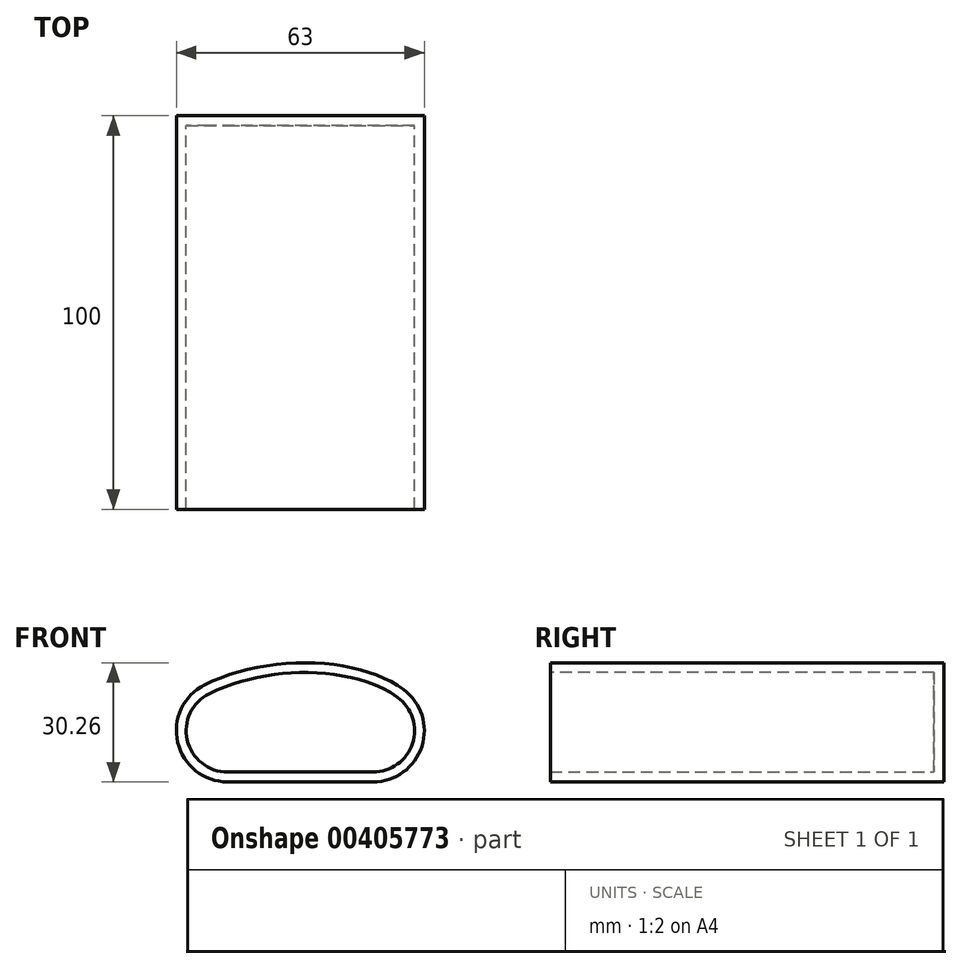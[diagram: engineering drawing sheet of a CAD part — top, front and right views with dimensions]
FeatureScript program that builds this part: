
annotation { "Feature Type Name" : "Feature", "Feature Type Description" : "" }
export const myFeature = defineFeature(function(context is Context, id is Id, definition is map)
    precondition{}
    {
        {
            var Q0;
            Q0=qCreatedBy(makeId("Front.planeOp"),FACE);
            var sketch = newSketch(context, id + "F0", { "sketchPlane" : qUnion([Q0])});
            skLineSegment(sketch, "E0", {"start": v(-15.79, 0) * mm, "end": v(21.21, 0) * mm});
            skCircle(sketch, "E1", {"center": v(-15.79, 0) * mm, "radius": 13 * mm});
            skCircle(sketch, "E2", {"center": v(21.21, 0) * mm, "radius": 13 * mm});
            skLineSegment(sketch, "E3", {"start": v(-15.79, 13) * mm, "end": v(21.21, 13) * mm});
            skLineSegment(sketch, "E4", {"start": v(2.71, 13) * mm, "end": v(2.71, -19) * mm});
            skPoint(sketch, "E4.endSnap0", {"position": v(2.71, 0) * mm});
            skEllipticalArc(sketch, "E5", {});
            skEllipse(sketch, "E6", {"center": v(2.71, -3) * mm, "majorRadius": 38.06 * mm, "minorRadius": 19.07 * mm, "majorAxis": v(-1, 0)});
            skLineSegment(sketch, "E7", {"start": v(-15.79, -13) * mm, "end": v(21.21, -13) * mm});
            const initialGuessF0  = {"E5": [0, -0.0030846775043755774, -0.995807587902254, -0.09147266190668617, 0.03564085790991101, 0.020163519470908692, 3.71118552486752, 5.312678315633367]};
            skSetInitialGuess(sketch, initialGuessF0);
            skSolve(sketch);
        }
        {
            var Q0;
            {var subQ0=sQuery(id+"F0.wireOp",EDGE,"E5");var subQ1=sQuery(id+"F0.wireOp",EDGE,"E1");var subQ2=makeQuery(id+"F0.imprint","INTERSECT",VERTEX,{"derivedFrom":[subQ1,subQ0]});Q0=makeQuery(id+"F0.imprint","IMPRINT",FACE,{"disambiguationData":[TD([[makeQuery(id+"F0.imprint","IMPRINT",EDGE,{"disambiguationData":[TD([[subQ2,1.0]])],"derivedFrom":subQ1}),-1.0]])]});}
            var Q1;
            {var subQ0=sQuery(id+"F0.wireOp",EDGE,"E5");var subQ1=sQuery(id+"F0.wireOp",EDGE,"E2");var subQ2=makeQuery(id+"F0.imprint","INTERSECT",VERTEX,{"derivedFrom":[subQ1,subQ0]});Q1=makeQuery(id+"F0.imprint","IMPRINT",FACE,{"disambiguationData":[TD([[makeQuery(id+"F0.imprint","IMPRINT",EDGE,{"disambiguationData":[TD([[subQ2,-1.0]])],"derivedFrom":subQ1}),-1.0]])]});}
            var Q2;
            {var subQ0=sQuery(id+"F0.wireOp",EDGE,"E6");var subQ1=sQuery(id+"F0.wireOp",EDGE,"E5");var subQ2=makeQuery(id+"F0.imprint","INTERSECT",VERTEX,{"disambiguationData":[OD(0.0)],"derivedFrom":[subQ1,subQ0]});Q2=makeQuery(id+"F0.imprint","IMPRINT",FACE,{"disambiguationData":[TD([[makeQuery(id+"F0.imprint","IMPRINT",EDGE,{"disambiguationData":[TD([[subQ2,-1.0]])],"derivedFrom":subQ1}),1.0]])]});}
            var Q3;
            {var subQ0=sQuery(id+"F0.wireOp",EDGE,"E1");var subQ4=makeQuery(id+"F0.imprint","INTERSECT",VERTEX,{"derivedFrom":[subQ0,sQuery(id+"F0.wireOp",EDGE,"E3")]});Q3=makeQuery(id+"F0.imprint","IMPRINT",FACE,{"disambiguationData":[TD([[makeQuery(id+"F0.imprint","IMPRINT",EDGE,{"disambiguationData":[TD([[subQ4,1.0]])],"derivedFrom":subQ0}),1.0]])]});}
            var Q4;
            {var subQ0=sQuery(id+"F0.wireOp",EDGE,"E2");var subQ5=makeQuery(id+"F0.imprint","INTERSECT",VERTEX,{"derivedFrom":[subQ0,sQuery(id+"F0.wireOp",EDGE,"E5")]});Q4=makeQuery(id+"F0.imprint","IMPRINT",FACE,{"disambiguationData":[TD([[makeQuery(id+"F0.imprint","IMPRINT",EDGE,{"disambiguationData":[TD([[subQ5,-1.0]])],"derivedFrom":subQ0}),1.0]])]});}
            var Q5;
            {var subQ0=sQuery(id+"F0.wireOp",EDGE,"E3");var subQ1=sQuery(id+"F0.wireOp",EDGE,"E1");var subQ2=makeQuery(id+"F0.imprint","INTERSECT",VERTEX,{"derivedFrom":[subQ1,subQ0]});Q5=makeQuery(id+"F0.imprint","IMPRINT",FACE,{"disambiguationData":[TD([[makeQuery(id+"F0.imprint","IMPRINT",EDGE,{"disambiguationData":[TD([[subQ2,-1.0]])],"derivedFrom":subQ1}),-1.0]])]});}
            var Q6;
            {var subQ0=sQuery(id+"F0.wireOp",EDGE,"E2");var subQ1=sQuery(id+"F0.wireOp",EDGE,"E0");var subQ2=makeQuery(id+"F0.imprint","INTERSECT",VERTEX,{"derivedFrom":[subQ1,subQ0]});Q6=makeQuery(id+"F0.imprint","IMPRINT",FACE,{"disambiguationData":[TD([[makeQuery(id+"F0.imprint","IMPRINT",EDGE,{"disambiguationData":[TD([[subQ2,1.0]])],"derivedFrom":subQ1}),1.0]])]});}
            var Q7;
            {var subQ0=sQuery(id+"F0.wireOp",EDGE,"E1");var subQ1=sQuery(id+"F0.wireOp",EDGE,"E0");var subQ2=makeQuery(id+"F0.imprint","INTERSECT",VERTEX,{"derivedFrom":[subQ1,subQ0]});Q7=makeQuery(id+"F0.imprint","IMPRINT",FACE,{"disambiguationData":[TD([[makeQuery(id+"F0.imprint","IMPRINT",EDGE,{"disambiguationData":[TD([[subQ2,-1.0]])],"derivedFrom":subQ1}),1.0]])]});}
            var Q8;
            {var subQ0=sQuery(id+"F0.wireOp",EDGE,"E1");var subQ1=sQuery(id+"F0.wireOp",EDGE,"E0");var subQ2=makeQuery(id+"F0.imprint","INTERSECT",VERTEX,{"derivedFrom":[subQ1,subQ0]});Q8=makeQuery(id+"F0.imprint","IMPRINT",FACE,{"disambiguationData":[TD([[makeQuery(id+"F0.imprint","IMPRINT",EDGE,{"disambiguationData":[TD([[subQ2,-1.0]])],"derivedFrom":subQ1}),-1.0]])]});}
            var Q9;
            {var subQ0=sQuery(id+"F0.wireOp",EDGE,"E2");var subQ1=sQuery(id+"F0.wireOp",EDGE,"E0");var subQ2=makeQuery(id+"F0.imprint","INTERSECT",VERTEX,{"derivedFrom":[subQ1,subQ0]});Q9=makeQuery(id+"F0.imprint","IMPRINT",FACE,{"disambiguationData":[TD([[makeQuery(id+"F0.imprint","IMPRINT",EDGE,{"disambiguationData":[TD([[subQ2,1.0]])],"derivedFrom":subQ1}),-1.0]])]});}
            extrude(context, id + "F1", {"entities" : qUnion([Q0, Q1, Q2, Q3, Q4, Q5, Q6, Q7, Q8, Q9]), "depth" : 100 * mm});
        }
        {
            var Q0;
            Q0=makeQuery(id+"F1.opExtrude","CAP_FACE",FACE,{"disambiguationData":[OSD([sQuery(id+"F0.wireOp",EDGE,"E1"),sQuery(id+"F0.wireOp",EDGE,"E2"),sQuery(id+"F0.wireOp",EDGE,"E5"),sQuery(id+"F0.wireOp",EDGE,"E7")])],"isStart":false});
            shell(context, id + "F2", {"entities" : qUnion([Q0]), "thickness" : 2.5 * mm});
        }
    });
